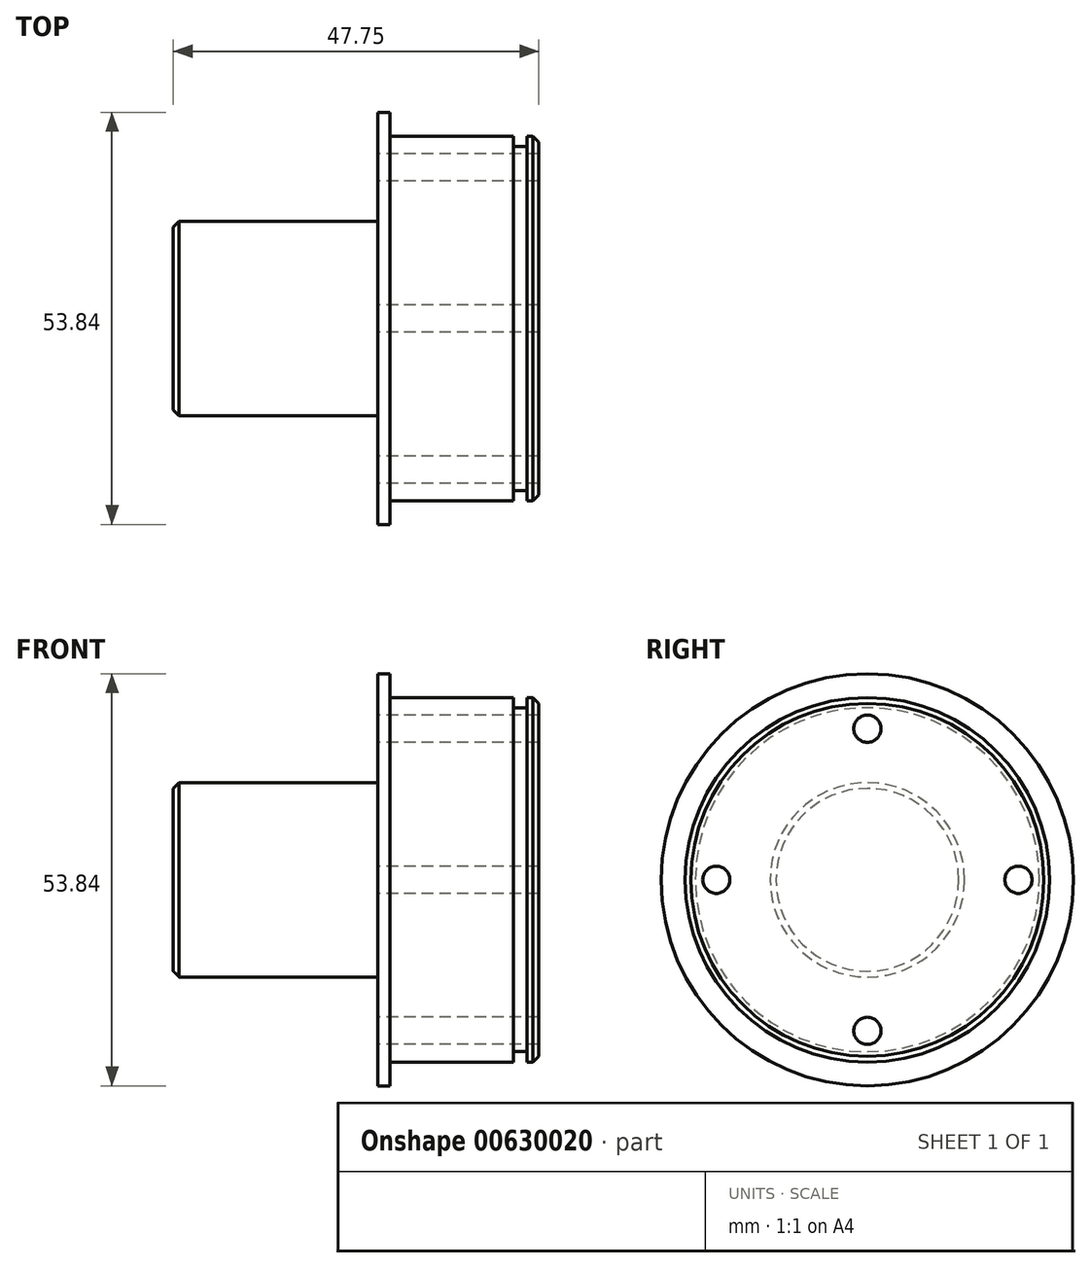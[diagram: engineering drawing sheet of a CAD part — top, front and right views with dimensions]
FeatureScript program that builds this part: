
annotation { "Feature Type Name" : "Feature", "Feature Type Description" : "" }
export const myFeature = defineFeature(function(context is Context, id is Id, definition is map)
    precondition{}
    {
        {
            var Q0;
            Q0=qCreatedBy(makeId("Right.planeOp"),FACE);
            var sketch = newSketch(context, id + "F0", { "sketchPlane" : qUnion([Q0])});
            skCircle(sketch, "E0", {"center": v(0, 0) * mm, "radius": 12.7 * mm});
            skSolve(sketch);
        }
        {
            var Q0;
            Q0=makeQuery(id+"F0.imprint","IMPRINT",FACE,{"disambiguationData":[TD([[makeQuery(id+"F0.imprint","IMPRINT",EDGE,{"derivedFrom":sQuery(id+"F0.wireOp",EDGE,"E0")}),1.0]])]});
            extrude(context, id + "F1", {"entities" : qUnion([Q0]), "depth" : 26.72 * mm, "offsetDistance" : 25.4 * mm});
        }
        {
            var Q0;
            Q0=makeQuery(id+"F1.opExtrude","CAP_FACE",FACE,{"disambiguationData":[OSD([sQuery(id+"F0.wireOp",EDGE,"E0")])],"isStart":false});
            var sketch = newSketch(context, id + "F2", { "sketchPlane" : qUnion([Q0])});
            skCircle(sketch, "E1", {"center": v(0, 0) * mm, "radius": 26.92 * mm});
            skSolve(sketch);
        }
        {
            var Q0;
            Q0=makeQuery(id+"F2.imprint","IMPRINT",FACE,{"disambiguationData":[TD([[makeQuery(id+"F2.imprint","IMPRINT",EDGE,{"derivedFrom":sQuery(id+"F2.wireOp",EDGE,"E1")}),1.0]])]});
            var Q1;
            Q1=makeQuery(id+"F2.imprint","IMPRINT",FACE,{"disambiguationData":[TD([[makeQuery(id+"F2.imprint","IMPRINT",EDGE,{"derivedFrom":makeQuery(id+"F1.opExtrude","CAP_EDGE",EDGE,{"disambiguationData":[OSD([sQuery(id+"F0.wireOp",EDGE,"E0")])],"isStart":false})}),1.0]])]});
            extrude(context, id + "F3", {"entities" : qUnion([Q0, Q1]), "operationType" : NewBodyOperationType.ADD, "depth" : 1.57 * mm, "offsetDistance" : 25.4 * mm});
        }
        {
            var Q0;
            Q0=makeQuery(id+"F3.opExtrude","CAP_FACE",FACE,{"disambiguationData":[OSD([sQuery(id+"F2.wireOp",EDGE,"E1")])],"isStart":false});
            var sketch = newSketch(context, id + "F4", { "sketchPlane" : qUnion([Q0])});
            skCircle(sketch, "E2", {"center": v(0, 0) * mm, "radius": 23.81 * mm});
            skSolve(sketch);
        }
        {
            var Q0;
            Q0=makeQuery(id+"F4.imprint","IMPRINT",FACE,{"disambiguationData":[TD([[makeQuery(id+"F4.imprint","IMPRINT",EDGE,{"derivedFrom":sQuery(id+"F4.wireOp",EDGE,"E2")}),1.0]])]});
            extrude(context, id + "F5", {"entities" : qUnion([Q0]), "operationType" : NewBodyOperationType.ADD, "depth" : 16.15 * mm, "offsetDistance" : 25.4 * mm});
        }
        {
            var Q0;
            Q0=makeQuery(id+"F5.opExtrude","CAP_FACE",FACE,{"disambiguationData":[OSD([sQuery(id+"F4.wireOp",EDGE,"E2")])],"isStart":false});
            var sketch = newSketch(context, id + "F6", { "sketchPlane" : qUnion([Q0])});
            skCircle(sketch, "E3", {"center": v(0, 0) * mm, "radius": 22.47 * mm});
            skSolve(sketch);
        }
        {
            var Q0;
            Q0=makeQuery(id+"F6.imprint","IMPRINT",FACE,{"disambiguationData":[TD([[makeQuery(id+"F6.imprint","IMPRINT",EDGE,{"derivedFrom":sQuery(id+"F6.wireOp",EDGE,"E3")}),1.0]])]});
            extrude(context, id + "F7", {"entities" : qUnion([Q0]), "operationType" : NewBodyOperationType.ADD, "depth" : 1.73 * mm, "offsetDistance" : 25.4 * mm});
        }
        {
            var Q0;
            Q0=makeQuery(id+"F7.opExtrude","CAP_FACE",FACE,{"disambiguationData":[OSD([sQuery(id+"F6.wireOp",EDGE,"E3")])],"isStart":false});
            var sketch = newSketch(context, id + "F8", { "sketchPlane" : qUnion([Q0])});
            skCircle(sketch, "E4", {"center": v(0, 0) * mm, "radius": 23.81 * mm});
            skSolve(sketch);
        }
        {
            var Q0;
            Q0 = qSketchRegion(id + "F8", true);
            extrude(context, id + "F9", {"entities" : qUnion([Q0]), "operationType" : NewBodyOperationType.ADD, "depth" : 1.57 * mm, "offsetDistance" : 25.4 * mm});
        }
        {
            var Q0;
            Q0=makeQuery(id+"F9.opExtrude","CAP_EDGE",EDGE,{"disambiguationData":[OSD([sQuery(id+"F8.wireOp",EDGE,"E4")])],"isStart":false});
            chamfer(context, id + "F10", {"entities" : qUnion([Q0]), "width" : 0.76 * mm, "tangentPropagation" : true});
        }
        {
            var Q0;
            Q0=makeQuery(id+"F1.opExtrude","CAP_EDGE",EDGE,{"disambiguationData":[OSD([sQuery(id+"F0.wireOp",EDGE,"E0")])],"isStart":true});
            chamfer(context, id + "F11", {"entities" : qUnion([Q0]), "width" : 0.76 * mm, "tangentPropagation" : true});
        }
        {
            var Q0;
            Q0=makeQuery(id+"F3.opExtrude","CAP_FACE",FACE,{"disambiguationData":[OSD([sQuery(id+"F2.wireOp",EDGE,"E1")])],"isStart":true});
            var sketch = newSketch(context, id + "F12", { "sketchPlane" : qUnion([Q0])});
            skCircle(sketch, "E5", {"center": v(0, 0) * mm, "radius": 19.74 * mm, "construction": true});
            skCircle(sketch, "E6", {"center": v(0, 19.74) * mm, "radius": 1.78 * mm});
            skCircle(sketch, "E7", {"center": v(19.74, 0) * mm, "radius": 1.78 * mm});
            skCircle(sketch, "E8", {"center": v(0, -19.74) * mm, "radius": 1.78 * mm});
            skCircle(sketch, "E9", {"center": v(-19.74, 0) * mm, "radius": 1.78 * mm});
            skSolve(sketch);
        }
        {
            var Q0;
            Q0=makeQuery(id+"F12.imprint","IMPRINT",FACE,{"disambiguationData":[TD([[makeQuery(id+"F12.imprint","IMPRINT",EDGE,{"derivedFrom":sQuery(id+"F12.wireOp",EDGE,"E6")}),1.0]])]});
            var Q1;
            Q1=makeQuery(id+"F12.imprint","IMPRINT",FACE,{"disambiguationData":[TD([[makeQuery(id+"F12.imprint","IMPRINT",EDGE,{"derivedFrom":sQuery(id+"F12.wireOp",EDGE,"E7")}),1.0]])]});
            var Q2;
            Q2=makeQuery(id+"F12.imprint","IMPRINT",FACE,{"disambiguationData":[TD([[makeQuery(id+"F12.imprint","IMPRINT",EDGE,{"derivedFrom":sQuery(id+"F12.wireOp",EDGE,"E8")}),1.0]])]});
            var Q3;
            Q3=makeQuery(id+"F12.imprint","IMPRINT",FACE,{"disambiguationData":[TD([[makeQuery(id+"F12.imprint","IMPRINT",EDGE,{"derivedFrom":sQuery(id+"F12.wireOp",EDGE,"E9")}),1.0]])]});
            var Q4;
            Q4=sQuery(id+"F12.wireOp",EDGE,"E6");
            var Q5;
            Q5=sQuery(id+"F12.wireOp",EDGE,"E7");
            var Q6;
            Q6=sQuery(id+"F12.wireOp",EDGE,"E8");
            var Q7;
            Q7=sQuery(id+"F12.wireOp",EDGE,"E9");
            extrude(context, id + "F13", {"entities" : qUnion([Q0, Q1, Q2, Q3]), "operationType" : NewBodyOperationType.REMOVE, "surfaceEntities" : qUnion([Q4, Q5, Q6, Q7]), "endBound" : BoundingType.THROUGH_ALL, "oppositeDirection" : true, "depth" : 25.4 * mm, "offsetDistance" : 25.4 * mm});
        }
    });
